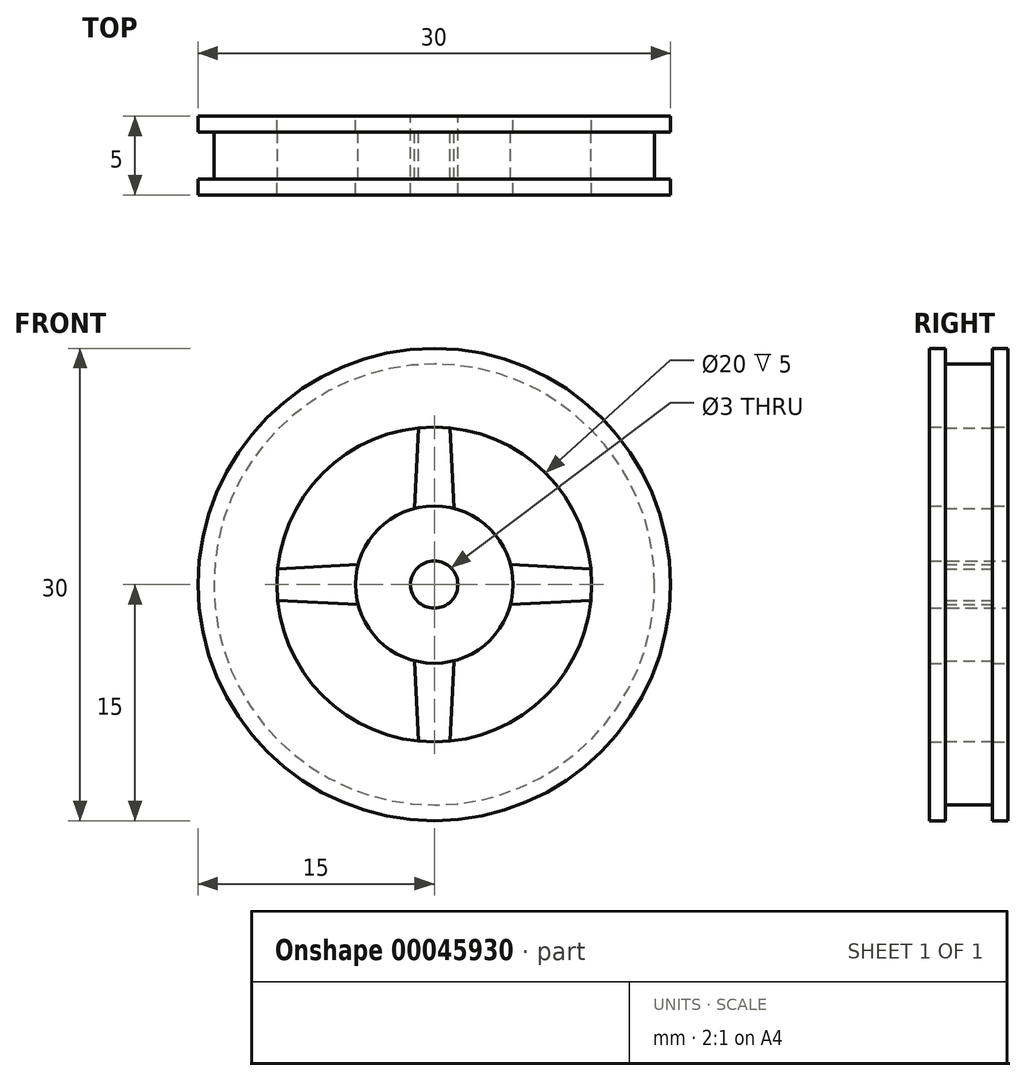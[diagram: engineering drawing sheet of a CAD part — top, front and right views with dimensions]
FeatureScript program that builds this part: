
annotation { "Feature Type Name" : "Feature", "Feature Type Description" : "" }
export const myFeature = defineFeature(function(context is Context, id is Id, definition is map)
    precondition{}
    {
        {
            var Q0;
            Q0=qCreatedBy(makeId("Front.planeOp"),FACE);
            var sketch = newSketch(context, id + "F0", { "sketchPlane" : qUnion([Q0])});
            skCircle(sketch, "E0", {"center": v(0, 0) * mm, "radius": 15 * mm});
            skCircle(sketch, "E1", {"center": v(0, 0) * mm, "radius": 5 * mm});
            skCircle(sketch, "E2", {"center": v(0, 0) * mm, "radius": 10 * mm});
            skLineSegment(sketch, "E3", {"start": v(-1, 9.95) * mm, "end": v(-1.27, 4.84) * mm});
            skLineSegment(sketch, "E4.MirrorCS", {"start": v(1, 9.95) * mm, "end": v(1.27, 4.84) * mm});
            skCircle(sketch, "E5", {"center": v(0, 0) * mm, "radius": 1.5 * mm});
            skSolve(sketch);
        }
        {
            var Q0;
            Q0=makeQuery(id+"F0.imprint","IMPRINT",FACE,{"disambiguationData":[TD([[makeQuery(id+"F0.imprint","IMPRINT",EDGE,{"derivedFrom":sQuery(id+"F0.wireOp",EDGE,"E0")}),1.0]])]});
            var Q1;
            {var subQ0=sQuery(id+"F0.wireOp",EDGE,"E1");var subQ6=makeQuery(id+"F0.imprint","INTERSECT",VERTEX,{"derivedFrom":[subQ0,sQuery(id+"F0.wireOp",EDGE,"E4.MirrorCS")]});Q1=makeQuery(id+"F0.imprint","IMPRINT",FACE,{"disambiguationData":[TD([[makeQuery(id+"F0.imprint","IMPRINT",EDGE,{"disambiguationData":[TD([[subQ6,1.0]])],"derivedFrom":subQ0}),1.0]])]});}
            extrude(context, id + "F1", {"entities" : qUnion([Q0, Q1]), "endBound" : BoundingType.SYMMETRIC, "depth" : 5 * mm});
        }
        {
            var Q0;
            {var subQ2=sQuery(id+"F0.wireOp",EDGE,"E3");Q0=makeQuery(id+"F0.imprint","IMPRINT",FACE,{"disambiguationData":[TD([[makeQuery(id+"F0.imprint","IMPRINT",EDGE,{"derivedFrom":subQ2}),1.0]])]});}
            var Q1;
            {var subQ0=sQuery(id+"F0.wireOp",EDGE,"a0065997-0ea5-4488-a0a8-ca713c354754.2.3.0");Q1=makeQuery(id+"F0.imprint","IMPRINT",FACE,{"disambiguationData":[TD([[makeQuery(id+"F0.imprint","IMPRINT",EDGE,{"derivedFrom":subQ0}),1.0]])]});}
            var Q2;
            {var subQ2=sQuery(id+"F0.wireOp",EDGE,"0ea7f381-05c6-4072-8b97-b638ddb051bf.2.0");Q2=makeQuery(id+"F0.imprint","IMPRINT",FACE,{"disambiguationData":[TD([[makeQuery(id+"F0.imprint","IMPRINT",EDGE,{"derivedFrom":subQ2}),1.0]])]});}
            var Q3;
            {var subQ2=sQuery(id+"F0.wireOp",EDGE,"0ea7f381-05c6-4072-8b97-b638ddb051bf.1.0");Q3=makeQuery(id+"F0.imprint","IMPRINT",FACE,{"disambiguationData":[TD([[makeQuery(id+"F0.imprint","IMPRINT",EDGE,{"derivedFrom":subQ2}),1.0]])]});}
            extrude(context, id + "F2", {"entities" : qUnion([Q0, Q1, Q2, Q3]), "operationType" : NewBodyOperationType.ADD, "endBound" : BoundingType.SYMMETRIC, "depth" : 3 * mm});
        }
        {
            var Q0;
            Q0=qCreatedBy(makeId("Front.planeOp"),FACE);
            var sketch = newSketch(context, id + "F3", { "sketchPlane" : qUnion([Q0])});
            skCircle(sketch, "E6.0", {"center": v(0, 0) * mm, "radius": 15 * mm});
            skCircle(sketch, "E7.0", {"center": v(0, 0) * mm, "radius": 14 * mm});
            skSolve(sketch);
        }
        {
            var Q0;
            Q0 = qSketchRegion(id + "F3", true);
            var Q1;
            Q1=makeQuery(id+"F2.opExtrude","CAP_FACE",FACE,{"disambiguationData":[OSD([sQuery(id+"F0.wireOp",EDGE,"E1"),sQuery(id+"F0.wireOp",EDGE,"E2"),sQuery(id+"F0.wireOp",EDGE,"E3"),sQuery(id+"F0.wireOp",EDGE,"E4.MirrorCS")])],"isStart":false});
            var Q2;
            Q2=makeQuery(id+"F2.opExtrude","CAP_FACE",FACE,{"disambiguationData":[OSD([sQuery(id+"F0.wireOp",EDGE,"E1"),sQuery(id+"F0.wireOp",EDGE,"E2"),sQuery(id+"F0.wireOp",EDGE,"E3"),sQuery(id+"F0.wireOp",EDGE,"E4.MirrorCS")])],"isStart":true});
            extrude(context, id + "F4", {"entities" : qUnion([Q0]), "operationType" : NewBodyOperationType.REMOVE, "endBound" : BoundingType.UP_TO_SURFACE, "endBoundEntityFace" : qUnion([Q1]), "depth" : 3 * mm, "hasSecondDirection" : true, "secondDirectionBound" : SecondDirectionBoundingType.UP_TO_SURFACE, "secondDirectionOppositeDirection" : true, "secondDirectionBoundEntityFace" : qUnion([Q2]), "secondDirectionDepth" : 25 * mm});
        }
        {
            var Q0;
            Q0=makeQuery(id+"F1.opExtrude","SWEPT_BODY",BODY,{"disambiguationData":[OSD([sQuery(id+"F0.wireOp",EDGE,"E0"),sQuery(id+"F0.wireOp",EDGE,"E2")])]});
            var Q1;
            Q1=makeQuery(id+"F1.opExtrude","CAP_EDGE",EDGE,{"disambiguationData":[OSD([sQuery(id+"F0.wireOp",EDGE,"E2")])],"isStart":false});
            circularPattern(context, id + "F5", {"operationType" : NewBodyOperationType.ADD, "entities" : qUnion([Q0]), "axis" : qUnion([Q1]), "angle" : 90 * degree, "instanceCount" : 4});
        }
    });
